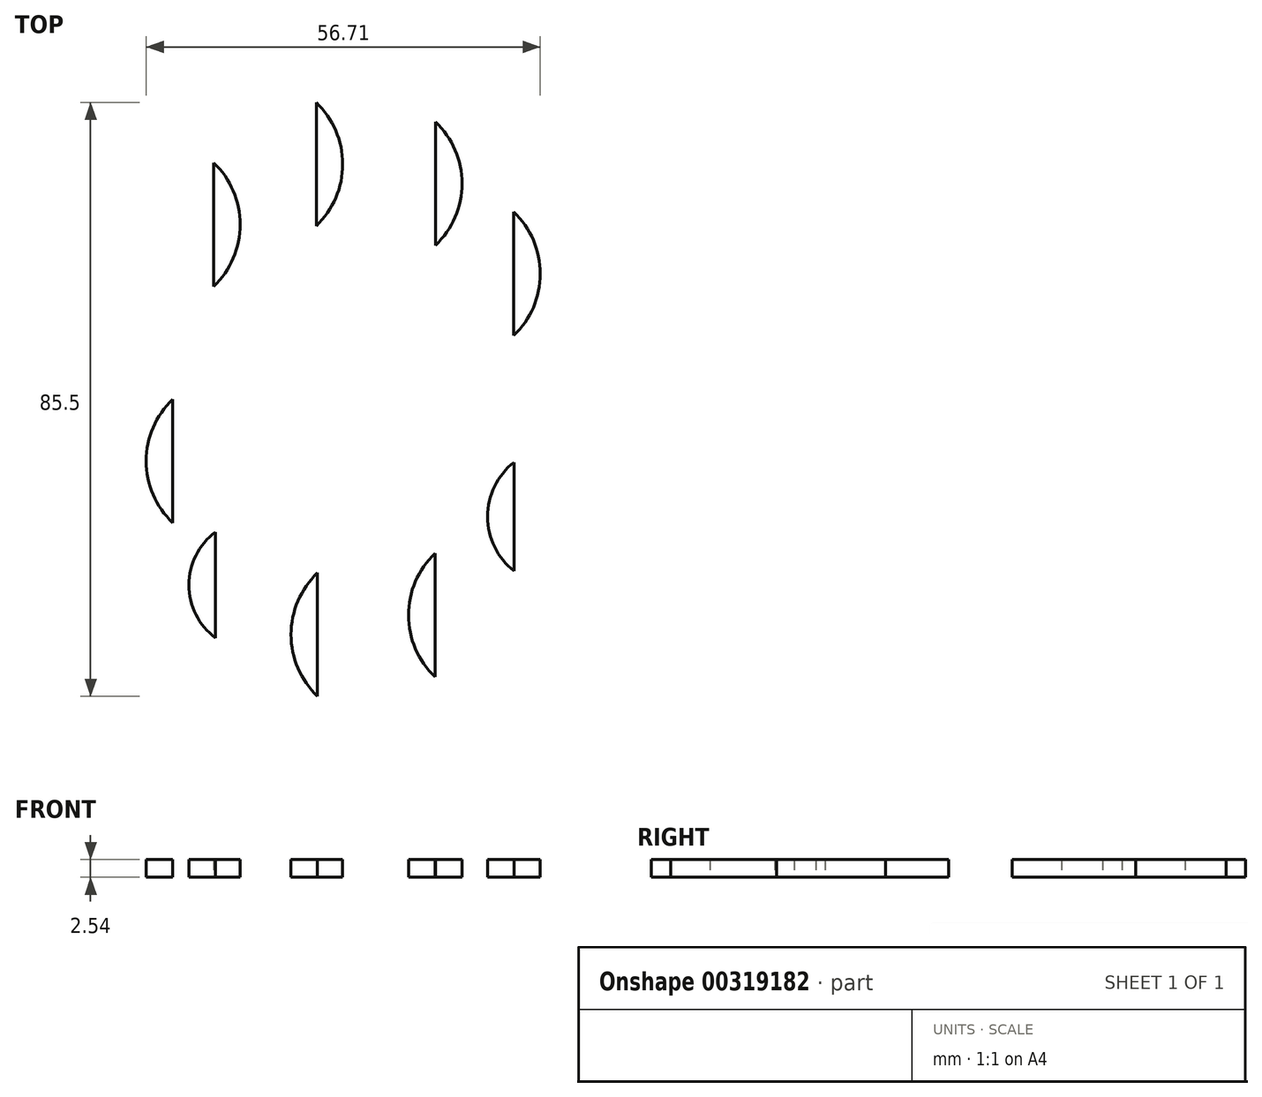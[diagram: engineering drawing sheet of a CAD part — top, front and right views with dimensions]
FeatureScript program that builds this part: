
annotation { "Feature Type Name" : "Feature", "Feature Type Description" : "" }
export const myFeature = defineFeature(function(context is Context, id is Id, definition is map)
    precondition{}
    {
        {
            var Q0;
            Q0=qCreatedBy(makeId("Top.planeOp"),FACE);
            var sketch = newSketch(context, id + "F0", { "sketchPlane" : qUnion([Q0])});
            skCircle(sketch, "E0", {"center": v(0, 0) * mm, "radius": 25.4 * mm, "construction": true});
            skLineSegment(sketch, "E1", {"start": v(-4.75, 24.95) * mm, "end": v(-4.75, 42.73) * mm});
            skLineSegment(sketch, "E2", {"start": v(12.42, 22.16) * mm, "end": v(12.42, 39.94) * mm});
            skLineSegment(sketch, "E3", {"start": v(23.69, 9.17) * mm, "end": v(23.69, 26.95) * mm});
            skLineSegment(sketch, "E4", {"start": v(23.73, -9.07) * mm, "end": v(23.73, -26.85) * mm});
            skLineSegment(sketch, "E5", {"start": v(12.34, -22.2) * mm, "end": v(12.34, -39.98) * mm});
            skLineSegment(sketch, "E6", {"start": v(-4.56, -24.99) * mm, "end": v(-4.56, -42.77) * mm});
            skLineSegment(sketch, "E7", {"start": v(-19.26, -16.56) * mm, "end": v(-19.26, -34.34) * mm});
            skLineSegment(sketch, "E8", {"start": v(-25.4, 0) * mm, "end": v(-25.4, -17.78) * mm});
            skLineSegment(sketch, "E9", {"start": v(-19.5, 16.27) * mm, "end": v(-19.5, 34.05) * mm});
            skArc(sketch, "E10", {"start": v(-19.5, 16.27) * mm, "mid": v(-15.7, 25.16) * mm, "end": v(-19.5, 34.05) * mm});
            skArc(sketch, "E11", {"start": v(-4.75, 24.95) * mm, "mid": v(-0.94, 33.84) * mm, "end": v(-4.75, 42.73) * mm});
            skArc(sketch, "E12", {"start": v(12.42, 22.16) * mm, "mid": v(16.23, 31.05) * mm, "end": v(12.42, 39.94) * mm});
            skArc(sketch, "E13", {"start": v(23.69, 9.17) * mm, "mid": v(27.5, 18.06) * mm, "end": v(23.69, 26.95) * mm});
            skArc(sketch, "E14", {"start": v(23.73, -9.07) * mm, "mid": v(19.95, -17.75) * mm, "end": v(25.16, -25.66) * mm});
            skArc(sketch, "E15", {"start": v(12.34, -22.2) * mm, "mid": v(8.53, -31.09) * mm, "end": v(12.34, -39.98) * mm});
            skArc(sketch, "E16", {"start": v(-4.56, -24.99) * mm, "mid": v(-8.37, -33.88) * mm, "end": v(-4.56, -42.77) * mm});
            skArc(sketch, "E17", {"start": v(-9.38, -18.17) * mm, "mid": v(-21.67, -21.76) * mm, "end": v(-19.26, -34.34) * mm});
            skArc(sketch, "E18", {"start": v(-25.4, 0) * mm, "mid": v(-29.21, -8.9) * mm, "end": v(-25.4, -17.78) * mm});
            skSolve(sketch);
        }
        {
            var Q0;
            Q0 = qSketchRegion(id + "F0", true);
            extrude(context, id + "F1", {"entities" : qUnion([Q0]), "endBound" : BoundingType.SYMMETRIC, "depth" : 2.54 * mm});
        }
    });
